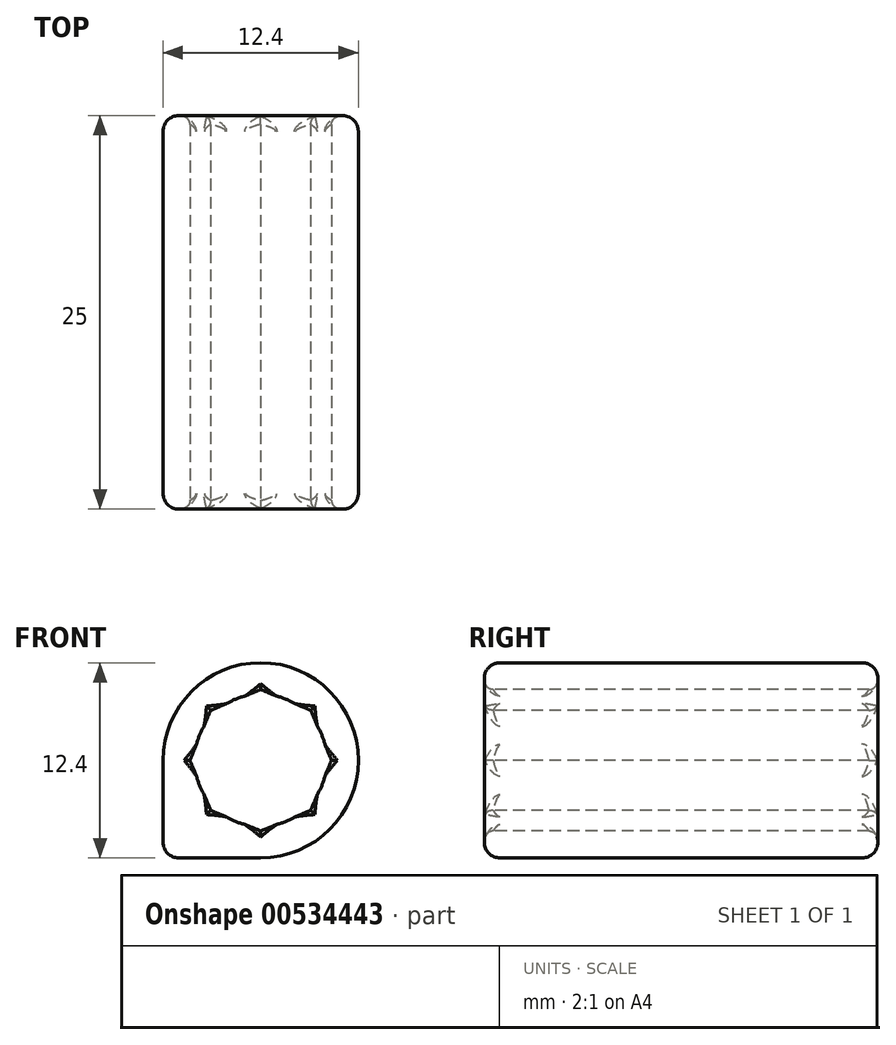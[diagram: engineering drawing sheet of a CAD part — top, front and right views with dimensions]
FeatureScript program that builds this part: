
annotation { "Feature Type Name" : "Feature", "Feature Type Description" : "" }
export const myFeature = defineFeature(function(context is Context, id is Id, definition is map)
    precondition{}
    {
        {
            var Q0;
            Q0=qCreatedBy(makeId("Front.planeOp"),FACE);
            var sketch = newSketch(context, id + "F0", { "sketchPlane" : qUnion([Q0])});
            skCircle(sketch, "E0", {"center": v(6.2, 6.2) * mm, "radius": 4.2 * mm});
            skCircle(sketch, "E1", {"center": v(6.2, 6.2) * mm, "radius": 6.2 * mm});
            skLineSegment(sketch, "E2", {"start": v(0, 0) * mm, "end": v(0, 6.2) * mm});
            skLineSegment(sketch, "E3", {"start": v(0, 0) * mm, "end": v(6.2, 0) * mm});
            skSolve(sketch);
        }
        {
            var Q0;
            Q0=makeQuery(id+"F0.imprint","IMPRINT",FACE,{"disambiguationData":[TD([[makeQuery(id+"F0.imprint","IMPRINT",EDGE,{"derivedFrom":sQuery(id+"F0.wireOp",EDGE,"E0")}),-1.0]])]});
            var Q1;
            {var subQ0=sQuery(id+"F0.wireOp",EDGE,"E2");Q1=makeQuery(id+"F0.imprint","IMPRINT",FACE,{"disambiguationData":[TD([[makeQuery(id+"F0.imprint","IMPRINT",EDGE,{"derivedFrom":subQ0}),-1.0]])]});}
            extrude(context, id + "F1", {"entities" : qUnion([Q0, Q1]), "oppositeDirection" : true, "depth" : 25 * mm});
        }
        {
            var Q0;
            Q0=makeQuery(id+"F1.opExtrude","CAP_FACE",FACE,{"disambiguationData":[OSD([sQuery(id+"F0.wireOp",EDGE,"E0"),sQuery(id+"F0.wireOp",EDGE,"E1"),sQuery(id+"F0.wireOp",EDGE,"E2"),sQuery(id+"F0.wireOp",EDGE,"E3")])],"isStart":false});
            var Q1;
            Q1=makeQuery(id+"F1.opExtrude","CAP_FACE",FACE,{"disambiguationData":[OSD([sQuery(id+"F0.wireOp",EDGE,"E0"),sQuery(id+"F0.wireOp",EDGE,"E1"),sQuery(id+"F0.wireOp",EDGE,"E2"),sQuery(id+"F0.wireOp",EDGE,"E3")])],"isStart":true});
            var Q2;
            Q2=makeQuery(id+"F1.opExtrude","SWEPT_EDGE",EDGE,{"disambiguationData":[OSD([sQuery(id+"F0.wireOp",EDGE,"E2"),sQuery(id+"F0.wireOp",EDGE,"E3")])]});
            fillet(context, id + "F2", {"entities" : qUnion([Q0, Q1, Q2]), "radius" : 1 * mm, "tangentPropagation" : true, "allowEdgeOverflow" : false});
        }
        {
            var Q0;
            Q0=qCreatedBy(makeId("Front.planeOp"),FACE);
            var sketch = newSketch(context, id + "F3", { "sketchPlane" : qUnion([Q0])});
            skCircle(sketch, "E4.cCircle", {"center": v(6.2, 6.2) * mm, "radius": 4.15 * mm, "construction": true});
            skLineSegment(sketch, "E4.0", {"start": v(9.38, 3.02) * mm, "end": v(6.2, 1.7) * mm});
            skLineSegment(sketch, "E4.1", {"start": v(6.2, 1.7) * mm, "end": v(3.02, 3.02) * mm});
            skLineSegment(sketch, "E4.2", {"start": v(3.02, 3.02) * mm, "end": v(1.7, 6.2) * mm});
            skLineSegment(sketch, "E4.3", {"start": v(1.7, 6.2) * mm, "end": v(3.02, 9.38) * mm});
            skLineSegment(sketch, "E4.4", {"start": v(3.02, 9.38) * mm, "end": v(6.2, 10.7) * mm});
            skLineSegment(sketch, "E4.5", {"start": v(6.2, 10.7) * mm, "end": v(9.38, 9.38) * mm});
            skLineSegment(sketch, "E4.6", {"start": v(9.38, 9.38) * mm, "end": v(10.7, 6.2) * mm});
            skLineSegment(sketch, "E4.7", {"start": v(10.7, 6.2) * mm, "end": v(9.38, 3.02) * mm});
            skPoint(sketch, "E4.0.midPoint", {"position": v(7.79, 2.37) * mm});
            skLineSegment(sketch, "E5", {"start": v(6.2, 0) * mm, "end": v(6.2, 12.4) * mm, "construction": true});
            skSolve(sketch);
        }
        {
            var Q0;
            Q0=qSketchRegion(id+"F3",true);
            extrude(context, id + "F4", {"entities" : qUnion([Q0]), "operationType" : NewBodyOperationType.REMOVE, "endBound" : BoundingType.THROUGH_ALL, "oppositeDirection" : true, "depth" : 25 * mm});
        }
        {
            var Q0;
            Q0=makeQuery(id+"F4.boolean.opBoolean","SPLIT",FACE,{"disambiguationData":[TD([makeQuery(id+"F4.opExtrude","SWEPT_FACE",FACE,{"disambiguationData":[OSD([sQuery(id+"F3.wireOp",EDGE,"E4.0")])]})])],"derivedFrom":makeQuery(id+"F1.opExtrude","SWEPT_FACE",FACE,{"disambiguationData":[OSD([sQuery(id+"F0.wireOp",EDGE,"E0")])]})});
            var Q1;
            Q1=makeQuery(id+"F4.boolean.opBoolean","SPLIT",FACE,{"disambiguationData":[TD([makeQuery(id+"F4.opExtrude","SWEPT_FACE",FACE,{"disambiguationData":[OSD([sQuery(id+"F3.wireOp",EDGE,"E4.7")])]})])],"derivedFrom":makeQuery(id+"F1.opExtrude","SWEPT_FACE",FACE,{"disambiguationData":[OSD([sQuery(id+"F0.wireOp",EDGE,"E0")])]})});
            var Q2;
            Q2=makeQuery(id+"F4.boolean.opBoolean","SPLIT",FACE,{"disambiguationData":[TD([makeQuery(id+"F4.opExtrude","SWEPT_FACE",FACE,{"disambiguationData":[OSD([sQuery(id+"F3.wireOp",EDGE,"E4.6")])]})])],"derivedFrom":makeQuery(id+"F1.opExtrude","SWEPT_FACE",FACE,{"disambiguationData":[OSD([sQuery(id+"F0.wireOp",EDGE,"E0")])]})});
            var Q3;
            Q3=makeQuery(id+"F4.boolean.opBoolean","SPLIT",FACE,{"disambiguationData":[TD([makeQuery(id+"F4.opExtrude","SWEPT_FACE",FACE,{"disambiguationData":[OSD([sQuery(id+"F3.wireOp",EDGE,"E4.5")])]})])],"derivedFrom":makeQuery(id+"F1.opExtrude","SWEPT_FACE",FACE,{"disambiguationData":[OSD([sQuery(id+"F0.wireOp",EDGE,"E0")])]})});
            var Q4;
            Q4=makeQuery(id+"F4.boolean.opBoolean","SPLIT",FACE,{"disambiguationData":[TD([makeQuery(id+"F4.opExtrude","SWEPT_FACE",FACE,{"disambiguationData":[OSD([sQuery(id+"F3.wireOp",EDGE,"E4.4")])]})])],"derivedFrom":makeQuery(id+"F1.opExtrude","SWEPT_FACE",FACE,{"disambiguationData":[OSD([sQuery(id+"F0.wireOp",EDGE,"E0")])]})});
            var Q5;
            Q5=makeQuery(id+"F4.boolean.opBoolean","SPLIT",FACE,{"disambiguationData":[TD([makeQuery(id+"F4.opExtrude","SWEPT_FACE",FACE,{"disambiguationData":[OSD([sQuery(id+"F3.wireOp",EDGE,"E4.3")])]})])],"derivedFrom":makeQuery(id+"F1.opExtrude","SWEPT_FACE",FACE,{"disambiguationData":[OSD([sQuery(id+"F0.wireOp",EDGE,"E0")])]})});
            var Q6;
            Q6=makeQuery(id+"F4.boolean.opBoolean","SPLIT",FACE,{"disambiguationData":[TD([makeQuery(id+"F4.opExtrude","SWEPT_FACE",FACE,{"disambiguationData":[OSD([sQuery(id+"F3.wireOp",EDGE,"E4.2")])]})])],"derivedFrom":makeQuery(id+"F1.opExtrude","SWEPT_FACE",FACE,{"disambiguationData":[OSD([sQuery(id+"F0.wireOp",EDGE,"E0")])]})});
            var Q7;
            Q7=makeQuery(id+"F4.boolean.opBoolean","SPLIT",FACE,{"disambiguationData":[TD([makeQuery(id+"F4.opExtrude","SWEPT_FACE",FACE,{"disambiguationData":[OSD([sQuery(id+"F3.wireOp",EDGE,"E4.1")])]})])],"derivedFrom":makeQuery(id+"F1.opExtrude","SWEPT_FACE",FACE,{"disambiguationData":[OSD([sQuery(id+"F0.wireOp",EDGE,"E0")])]})});
            fillet(context, id + "F5", {"entities" : qUnion([Q0, Q1, Q2, Q3, Q4, Q5, Q6, Q7]), "radius" : .5 * mm, "tangentPropagation" : true, "allowEdgeOverflow" : false});
        }
    });
